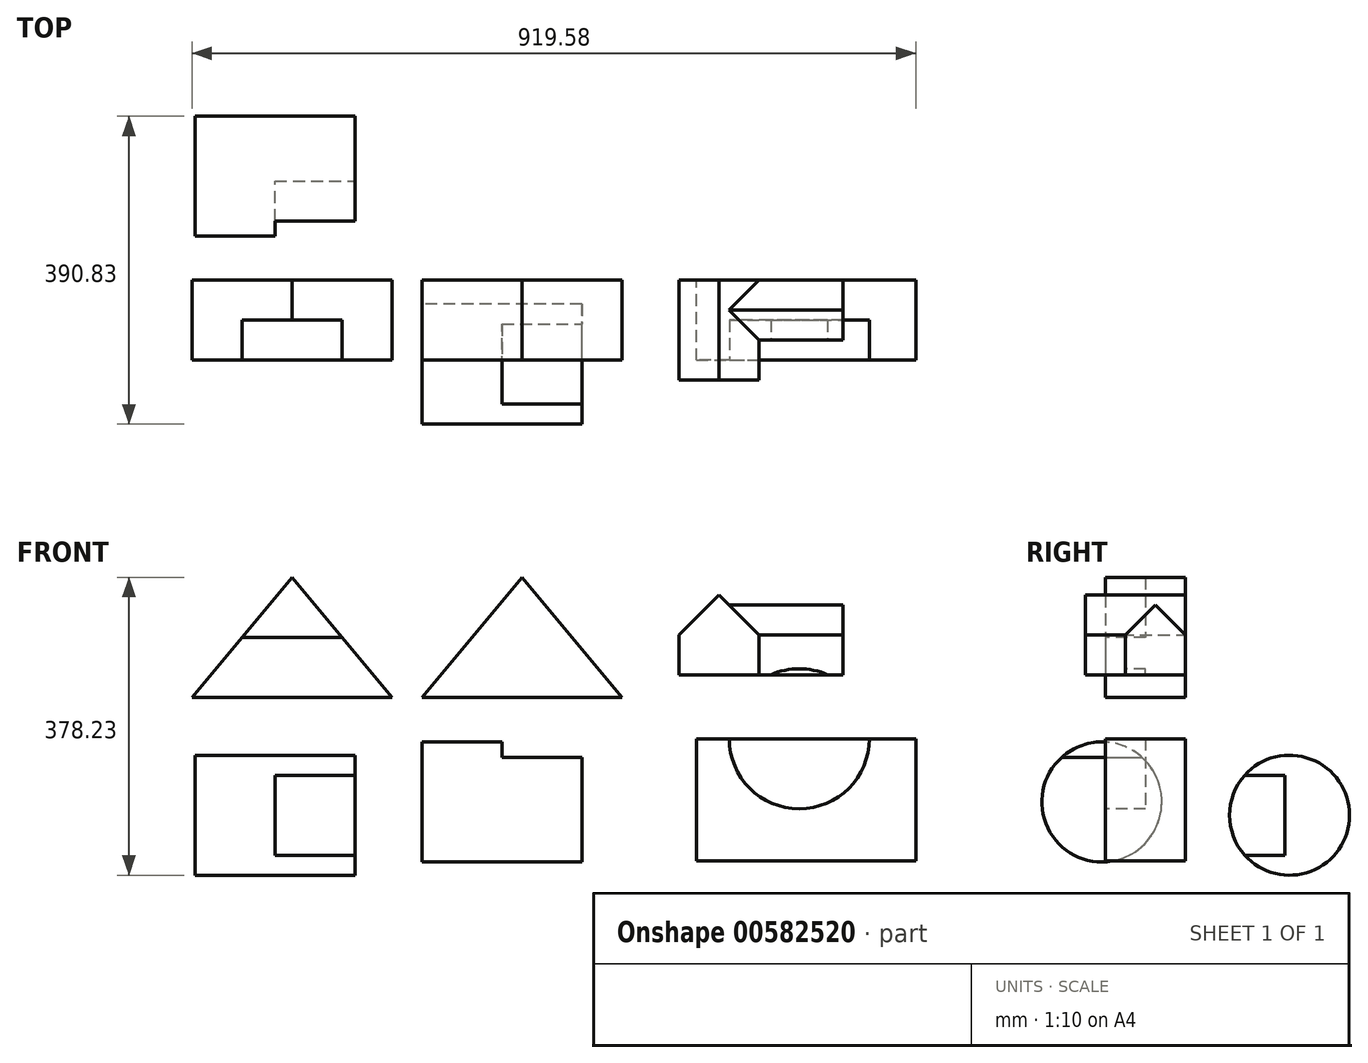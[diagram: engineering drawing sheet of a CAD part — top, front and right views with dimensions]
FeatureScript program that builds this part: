
annotation { "Feature Type Name" : "Feature", "Feature Type Description" : "" }
export const myFeature = defineFeature(function(context is Context, id is Id, definition is map)
    precondition{}
    {
        {
            var Q0;
            Q0=qCreatedBy(makeId("Front.planeOp"),FACE);
            var sketch = newSketch(context, id + "F0", { "sketchPlane" : qUnion([Q0])});
            skLineSegment(sketch, "E0", {"start": v(-292.36, 0) * mm, "end": v(-38.36, 0) * mm});
            skLineSegment(sketch, "E1", {"start": v(-38.36, 0) * mm, "end": v(-165.36, 152.4) * mm});
            skLineSegment(sketch, "E2", {"start": v(-165.36, 152.4) * mm, "end": v(-292.36, 0) * mm});
            skLineSegment(sketch, "E3", {"start": v(-165.36, 152.4) * mm, "end": v(-38.36, 0) * mm});
            skSolve(sketch);
        }
        {
            var Q0;
            Q0 = qSketchRegion(id + "F0", true);
            extrude(context, id + "F1", {"entities" : qUnion([Q0]), "depth" : 101.6 * mm, "offsetDistance" : 25.4 * mm});
        }
        {
            var Q0;
            Q0=makeQuery(id+"F1.opExtrude","CAP_FACE",FACE,{"disambiguationData":[OSD([sQuery(id+"F0.wireOp",EDGE,"E0"),sQuery(id+"F0.wireOp",EDGE,"E2"),sQuery(id+"F0.wireOp",EDGE,"E3")])],"isStart":false});
            var sketch = newSketch(context, id + "F2", { "sketchPlane" : qUnion([Q0])});
            skLineSegment(sketch, "E4", {"start": v(-228.86, 76.2) * mm, "end": v(-101.86, 76.2) * mm});
            skSolve(sketch);
        }
        {
            var Q0;
            Q0 = qSketchRegion(id + "F2", true);
            var Q1;
            {var subQ0=sQuery(id+"F2.wireOp",EDGE,"E4");Q1=makeQuery(id+"F2.imprint","IMPRINT",FACE,{"disambiguationData":[TD([[makeQuery(id+"F2.imprint","IMPRINT",EDGE,{"derivedFrom":subQ0}),1.0]])]});}
            extrude(context, id + "F3", {"entities" : qUnion([Q0, Q1]), "operationType" : NewBodyOperationType.REMOVE, "oppositeDirection" : true, "depth" : 50.8 * mm, "offsetDistance" : 25.4 * mm});
        }
        {
            var Q0;
            Q0=qCreatedBy(makeId("Front.planeOp"),FACE);
            var sketch = newSketch(context, id + "F4", { "sketchPlane" : qUnion([Q0])});
            skLineSegment(sketch, "E5", {"start": v(0, 0) * mm, "end": v(254, 0) * mm});
            skLineSegment(sketch, "E6", {"start": v(254, 0) * mm, "end": v(127, 152.4) * mm});
            skLineSegment(sketch, "E7", {"start": v(127, 152.4) * mm, "end": v(0, 0) * mm});
            skSolve(sketch);
        }
        {
            var Q0;
            Q0 = qSketchRegion(id + "F4", true);
            extrude(context, id + "F5", {"entities" : qUnion([Q0]), "depth" : 101.6 * mm, "offsetDistance" : 25.4 * mm});
        }
        {
            var Q0;
            Q0=qCreatedBy(makeId("Front.planeOp"),FACE);
            var sketch = newSketch(context, id + "F6", { "sketchPlane" : qUnion([Q0])});
            skLineSegment(sketch, "E8", {"start": v(326.61, 28.74) * mm, "end": v(326.61, 79.54) * mm});
            skLineSegment(sketch, "E9", {"start": v(326.61, 79.54) * mm, "end": v(377.41, 130.34) * mm});
            skLineSegment(sketch, "E10", {"start": v(377.41, 130.34) * mm, "end": v(428.21, 79.54) * mm});
            skLineSegment(sketch, "E11", {"start": v(428.21, 79.54) * mm, "end": v(428.21, 28.74) * mm});
            skLineSegment(sketch, "E12", {"start": v(326.61, 28.74) * mm, "end": v(428.21, 28.74) * mm});
            skSolve(sketch);
        }
        {
            var Q0;
            Q0 = qSketchRegion(id + "F6", true);
            extrude(context, id + "F7", {"entities" : qUnion([Q0]), "depth" : 127 * mm, "offsetDistance" : 25.4 * mm});
        }
        {
            var Q0;
            Q0 = qSketchRegion(id + "F6", true);
            extrude(context, id + "F8", {"entities" : qUnion([Q0]), "operationType" : NewBodyOperationType.ADD, "depth" : 127 * mm, "offsetDistance" : 25.4 * mm});
        }
        {
            var Q0;
            Q0=makeQuery(id+"F7.opExtrude","SWEPT_FACE",FACE,{"disambiguationData":[OSD([sQuery(id+"F6.wireOp",EDGE,"E11")])]});
            cPlane(context, id + "F9", {"entities" : qUnion([Q0]), "cplaneType" : CPlaneType.OFFSET, "offset" : 106.68 * mm, "width" : 152.4 * mm, "height" : 152.4 * mm});
        }
        {
            var Q0;
            Q0=qCreatedBy(id+"F9.planeOp",FACE);
            var sketch = newSketch(context, id + "F10", { "sketchPlane" : qUnion([Q0])});
            skLineSegment(sketch, "E13", {"start": v(0, 28.74) * mm, "end": v(-76.2, 28.74) * mm});
            skLineSegment(sketch, "E14", {"start": v(-76.2, 28.74) * mm, "end": v(-76.2, 79.54) * mm});
            skLineSegment(sketch, "E15", {"start": v(-76.2, 79.54) * mm, "end": v(-38.1, 117.64) * mm});
            skLineSegment(sketch, "E16", {"start": v(-38.1, 117.64) * mm, "end": v(0, 79.54) * mm});
            skLineSegment(sketch, "E17", {"start": v(0, 79.54) * mm, "end": v(0, 28.74) * mm});
            skSolve(sketch);
        }
        {
            var Q0;
            Q0=makeQuery(id+"F10.imprint","IMPRINT",FACE,{"disambiguationData":[TD([[makeQuery(id+"F10.imprint","IMPRINT",EDGE,{"derivedFrom":sQuery(id+"F10.wireOp",EDGE,"E13")}),-1.0]])]});
            extrude(context, id + "F11", {"entities" : qUnion([Q0]), "operationType" : NewBodyOperationType.ADD, "endBound" : BoundingType.UP_TO_NEXT, "oppositeDirection" : true, "depth" : 127 * mm, "offsetDistance" : 25.4 * mm});
        }
        {
            var Q0;
            Q0=qCreatedBy(makeId("Right.planeOp"),FACE);
            var sketch = newSketch(context, id + "F12", { "sketchPlane" : qUnion([Q0])});
            skCircle(sketch, "E18", {"center": v(-106.48, -132.76) * mm, "radius": 76.2 * mm});
            skSolve(sketch);
        }
        {
            var Q0;
            Q0=makeQuery(id+"F12.imprint","IMPRINT",FACE,{"disambiguationData":[TD([[makeQuery(id+"F12.imprint","IMPRINT",EDGE,{"derivedFrom":sQuery(id+"F12.wireOp",EDGE,"E18")}),1.0]])]});
            extrude(context, id + "F13", {"entities" : qUnion([Q0]), "depth" : 203.2 * mm, "offsetDistance" : 25.4 * mm});
        }
        {
            var Q0;
            Q0=makeQuery(id+"F13.opExtrude","CAP_FACE",FACE,{"disambiguationData":[OSD([sQuery(id+"F12.wireOp",EDGE,"E18")])],"isStart":false});
            var sketch = newSketch(context, id + "F14", { "sketchPlane" : qUnion([Q0])});
            skLineSegment(sketch, "E19", {"start": v(-157.28, -75.96) * mm, "end": v(-55.68, -75.96) * mm});
            skSolve(sketch);
        }
        {
            var Q0;
            {var subQ0=sQuery(id+"F14.wireOp",EDGE,"E19");Q0=makeQuery(id+"F14.imprint","IMPRINT",FACE,{"disambiguationData":[TD([[makeQuery(id+"F14.imprint","IMPRINT",EDGE,{"derivedFrom":subQ0}),1.0]])]});}
            extrude(context, id + "F15", {"entities" : qUnion([Q0]), "operationType" : NewBodyOperationType.REMOVE, "oppositeDirection" : true, "depth" : 101.6 * mm, "offsetDistance" : 25.4 * mm});
        }
        {
            var Q0;
            Q0=qCreatedBy(makeId("Right.planeOp"),FACE);
            cPlane(context, id + "F16", {"entities" : qUnion([Q0]), "cplaneType" : CPlaneType.OFFSET, "offset" : 288.54 * mm, "oppositeDirection" : true, "width" : 152.4 * mm, "height" : 152.4 * mm});
        }
        {
            var Q0;
            Q0=qCreatedBy(id+"F16.planeOp",FACE);
            var sketch = newSketch(context, id + "F17", { "sketchPlane" : qUnion([Q0])});
            skCircle(sketch, "E20", {"center": v(131.95, -149.63) * mm, "radius": 76.2 * mm});
            skSolve(sketch);
        }
        {
            var Q0;
            Q0=makeQuery(id+"F17.imprint","IMPRINT",FACE,{"disambiguationData":[TD([[makeQuery(id+"F17.imprint","IMPRINT",EDGE,{"derivedFrom":sQuery(id+"F17.wireOp",EDGE,"E20")}),1.0]])]});
            extrude(context, id + "F18", {"entities" : qUnion([Q0]), "depth" : 203.2 * mm, "offsetDistance" : 25.4 * mm});
        }
        {
            var Q0;
            Q0=makeQuery(id+"F18.opExtrude","CAP_FACE",FACE,{"disambiguationData":[OSD([sQuery(id+"F17.wireOp",EDGE,"E20")])],"isStart":false});
            var sketch = newSketch(context, id + "F19", { "sketchPlane" : qUnion([Q0])});
            skLineSegment(sketch, "E21", {"start": v(75.16, -98.83) * mm, "end": v(125.96, -98.83) * mm});
            skLineSegment(sketch, "E22", {"start": v(125.96, -98.83) * mm, "end": v(125.96, -200.43) * mm});
            skLineSegment(sketch, "E23", {"start": v(125.96, -200.43) * mm, "end": v(75.16, -200.43) * mm});
            skSolve(sketch);
        }
        {
            var Q0;
            Q0 = qSketchRegion(id + "F19", true);
            var Q1;
            {var subQ0=sQuery(id+"F19.wireOp",EDGE,"E21");Q1=makeQuery(id+"F19.imprint","IMPRINT",FACE,{"disambiguationData":[TD([[makeQuery(id+"F19.imprint","IMPRINT",EDGE,{"derivedFrom":subQ0}),-1.0]])]});}
            extrude(context, id + "F20", {"entities" : qUnion([Q0, Q1]), "operationType" : NewBodyOperationType.REMOVE, "oppositeDirection" : true, "depth" : 101.6 * mm, "offsetDistance" : 25.4 * mm});
        }
        {
            var Q0;
            Q0=qCreatedBy(makeId("Front.planeOp"),FACE);
            var sketch = newSketch(context, id + "F21", { "sketchPlane" : qUnion([Q0])});
            skLineSegment(sketch, "E24", {"start": v(348.34, -52.48) * mm, "end": v(348.34, -207.88) * mm});
            skLineSegment(sketch, "E25", {"start": v(348.34, -207.88) * mm, "end": v(627.22, -207.88) * mm});
            skLineSegment(sketch, "E26", {"start": v(627.22, -207.88) * mm, "end": v(627.22, -52.48) * mm});
            skLineSegment(sketch, "E27", {"start": v(627.22, -52.48) * mm, "end": v(348.34, -52.48) * mm});
            skSolve(sketch);
        }
        {
            var Q0;
            Q0=makeQuery(id+"F21.imprint","IMPRINT",FACE,{"disambiguationData":[TD([[makeQuery(id+"F21.imprint","IMPRINT",EDGE,{"derivedFrom":sQuery(id+"F21.wireOp",EDGE,"E24")}),1.0]])]});
            extrude(context, id + "F22", {"entities" : qUnion([Q0]), "depth" : 101.6 * mm, "offsetDistance" : 25.4 * mm});
        }
        {
            var Q0;
            Q0=makeQuery(id+"F22.opExtrude","CAP_FACE",FACE,{"disambiguationData":[OSD([sQuery(id+"F21.wireOp",EDGE,"E24"),sQuery(id+"F21.wireOp",EDGE,"E25"),sQuery(id+"F21.wireOp",EDGE,"E26"),sQuery(id+"F21.wireOp",EDGE,"E27")])],"isStart":false});
            var sketch = newSketch(context, id + "F23", { "sketchPlane" : qUnion([Q0])});
            skCircle(sketch, "E28", {"center": v(479.07, -52.48) * mm, "radius": 88.9 * mm});
            skSolve(sketch);
        }
        {
            var Q0;
            {var subQ0=sQuery(id+"F23.wireOp",EDGE,"E28");var subQ1=makeQuery(id+"F22.opExtrude","CAP_EDGE",EDGE,{"disambiguationData":[OSD([sQuery(id+"F21.wireOp",EDGE,"E27")])],"isStart":false});var subQ2=makeQuery(id+"F23.imprint","INTERSECT",VERTEX,{"disambiguationData":[OD(0.0)],"derivedFrom":[subQ1,subQ0]});Q0=makeQuery(id+"F23.imprint","IMPRINT",FACE,{"disambiguationData":[TD([[makeQuery(id+"F23.imprint","IMPRINT",EDGE,{"disambiguationData":[TD([[subQ2,1.0]])],"derivedFrom":subQ0}),1.0]])]});}
            var Q1;
            {var subQ0=sQuery(id+"F23.wireOp",EDGE,"E28");var subQ1=makeQuery(id+"F22.opExtrude","CAP_EDGE",EDGE,{"disambiguationData":[OSD([sQuery(id+"F21.wireOp",EDGE,"E27")])],"isStart":false});var subQ2=makeQuery(id+"F23.imprint","INTERSECT",VERTEX,{"disambiguationData":[OD(0.0)],"derivedFrom":[subQ1,subQ0]});Q1=makeQuery(id+"F23.imprint","IMPRINT",FACE,{"disambiguationData":[TD([[makeQuery(id+"F23.imprint","IMPRINT",EDGE,{"disambiguationData":[TD([[subQ2,-1.0]])],"derivedFrom":subQ0}),1.0]])]});}
            extrude(context, id + "F24", {"entities" : qUnion([Q0, Q1]), "operationType" : NewBodyOperationType.REMOVE, "oppositeDirection" : true, "depth" : 50.8 * mm, "offsetDistance" : 25.4 * mm});
        }
    });
